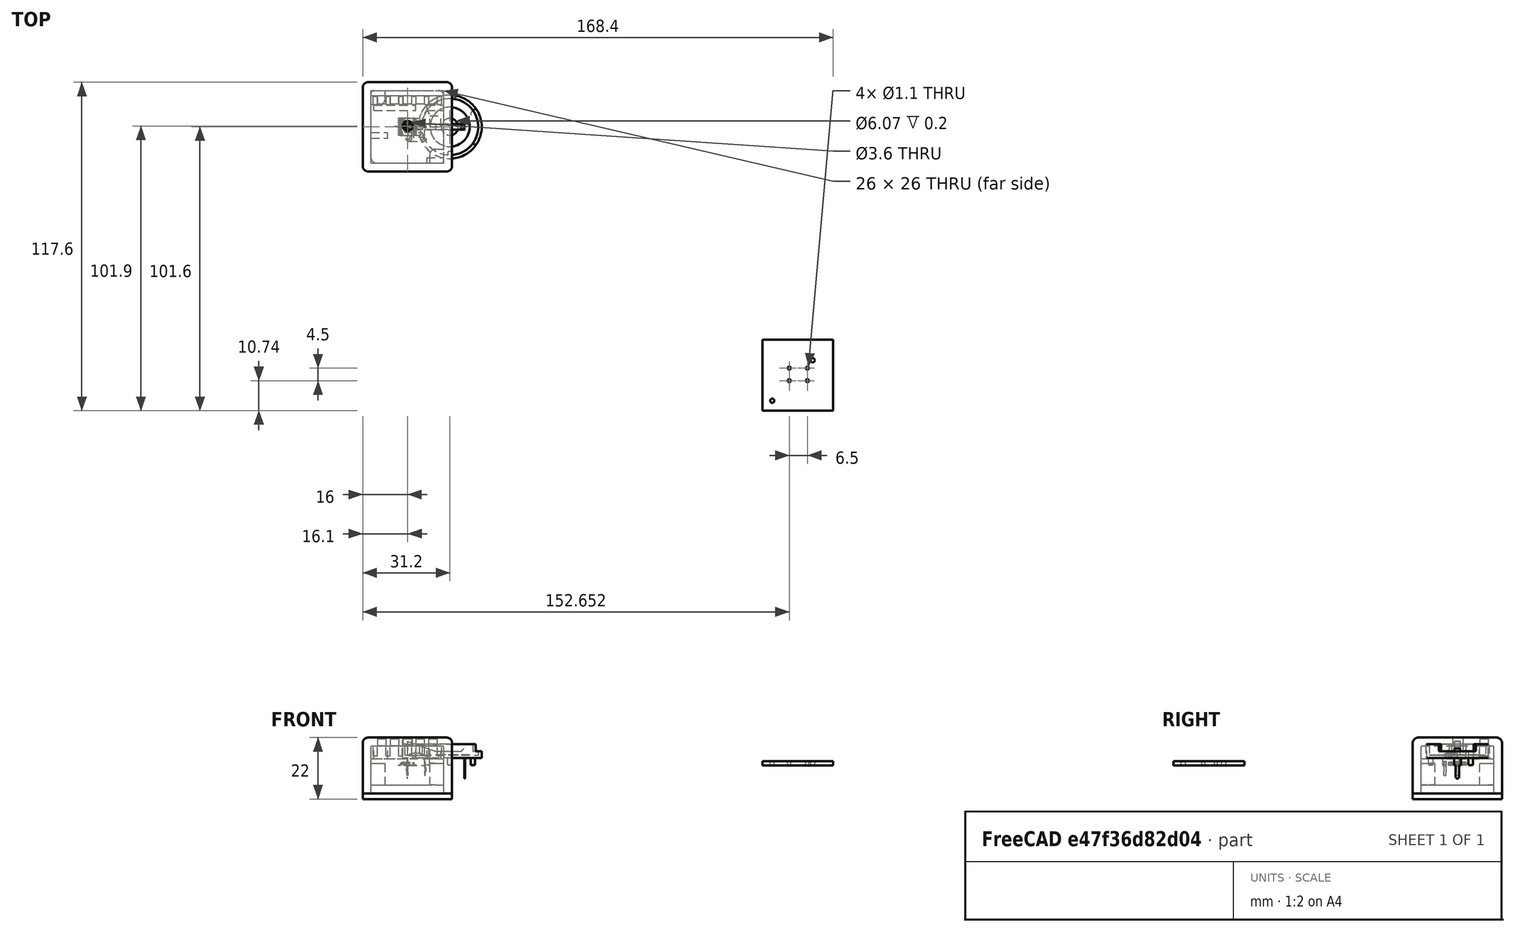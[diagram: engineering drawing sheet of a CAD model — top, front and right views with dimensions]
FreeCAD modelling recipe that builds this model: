
FCSTD DOCUMENT  (FreeCAD 0.18R16131 (Git))
Label: BoxSup
License: All rights reserved
LicenseURL: http://en.wikipedia.org/wiki/All_rights_reserved
objects: Part::Feature×30, App::Part×30, Part::Box×23, Part::Fillet×4, Part::Cut×3, Part::MultiFuse×3, Part::Cylinder×1
note: 64 computed .brp shape members not serialized (recipe doc carries the construction recipe); baked Part::Feature solids carry a one-line shape summary decoded from their .brp

FEATURE [Part::Box] Box  label="MainInside"
  AttacherType = Attacher::AttachEngine3D
  Height = 17
  Length = 26
  Placement = pos=(-13,-13,-10) rot=(0,0,1;0rad)
  Width = 26
FEATURE [Part::Box] Box001  label="MainOutside"
  AttacherType = Attacher::AttachEngine3D
  Height = 20
  Length = 32
  Placement = pos=(-16,-16,-10) rot=(0,0,1;0rad)
  Width = 32
FEATURE [Part::Feature] Part__Feature  label="SOLID"
  shape: bbox 2 x 1.25 x 1.1 mm, 50 faces (baked)
FEATURE [App::Part] LED_0805_2012Metric
  Group = -> [Part__Feature]
  License = CC BY 3.0
  LicenseURL = http://creativecommons.org/licenses/by/3.0/
  Origin = -> Origin
  Placement = pos=(144.272,-79.248,1.65) rot=(0,0,-1;1.5708rad)
FEATURE [Part::Feature] Part__Feature001  label="SOLID001"
  shape: bbox 7.174 x 6 x 7.8 mm, 105 faces (baked)
FEATURE [App::Part] SW_PUSH_6mm
  Group = -> [Part__Feature001]
  License = CC BY 3.0
  LicenseURL = http://creativecommons.org/licenses/by/3.0/
  Origin = -> Origin001
  Placement = pos=(136.652,-86.36,1.65) rot=(0,0,1;0rad)
FEATURE [Part::Feature] Part__Feature002  label="SOLID002"
  shape: bbox 1.6 x 0.8 x 0.45 mm, 26 faces (baked)
FEATURE [App::Part] R_0603_1608Metric
  Group = -> [Part__Feature002]
  License = CC BY 3.0
  LicenseURL = http://creativecommons.org/licenses/by/3.0/
  Origin = -> Origin002
  Placement = pos=(147.701,-98.679,1.65) rot=(0,0,1;0rad)
FEATURE [Part::Feature] Part__Feature003  label="SOLID003"
  shape: bbox 1.6 x 0.8 x 0.45 mm, 26 faces (baked)
FEATURE [App::Part] R_0603_1608Metric001
  Group = -> [Part__Feature003]
  License = CC BY 3.0
  LicenseURL = http://creativecommons.org/licenses/by/3.0/
  Origin = -> Origin003
  Placement = pos=(145.411,-99.187,1.65) rot=(0,0,1;1.5708rad)
FEATURE [Part::Feature] Part__Feature004  label="SOLID004"
  shape: bbox 6.4 x 6.5 x 1.2 mm, 336 faces (baked)
FEATURE [App::Part] TSSOP_20_4_4x6_5mm_P0_65mm
  Group = -> [Part__Feature004]
  License = CC BY 3.0
  LicenseURL = http://creativecommons.org/licenses/by/3.0/
  Origin = -> Origin004
  Placement = pos=(148.336,-93.81,1.65) rot=(0,0,1;1.5708rad)
FEATURE [Part::Feature] Part__Feature005  label="SOLID005"
  shape: bbox 2 x 1.25 x 1.1 mm, 50 faces (baked)
FEATURE [App::Part] LED_0805_2012Metric001
  Group = -> [Part__Feature005]
  License = CC BY 3.0
  LicenseURL = http://creativecommons.org/licenses/by/3.0/
  Origin = -> Origin005
  Placement = pos=(130.556,-79.248,1.65) rot=(0,0,-1;1.5708rad)
FEATURE [Part::Feature] Part__Feature006  label="SOLID006"
  shape: bbox 2 x 1.25 x 1.1 mm, 50 faces (baked)
FEATURE [App::Part] LED_0805_2012Metric002
  Group = -> [Part__Feature006]
  License = CC BY 3.0
  LicenseURL = http://creativecommons.org/licenses/by/3.0/
  Origin = -> Origin006
  Placement = pos=(135.128,-79.248,1.65) rot=(0,0,-1;1.5708rad)
FEATURE [Part::Feature] Part__Feature007  label="SOLID007"
  shape: bbox 2 x 1.25 x 1.1 mm, 50 faces (baked)
FEATURE [App::Part] LED_0805_2012Metric003
  Group = -> [Part__Feature007]
  License = CC BY 3.0
  LicenseURL = http://creativecommons.org/licenses/by/3.0/
  Origin = -> Origin007
  Placement = pos=(139.7,-79.248,1.65) rot=(0,0,-1;1.5708rad)
FEATURE [Part::Feature] Part__Feature008  label="SOLID008"
  shape: bbox 2 x 1.25 x 1.1 mm, 50 faces (baked)
FEATURE [App::Part] LED_0805_2012Metric004
  Group = -> [Part__Feature008]
  License = CC BY 3.0
  LicenseURL = http://creativecommons.org/licenses/by/3.0/
  Origin = -> Origin008
  Placement = pos=(148.844,-79.248,1.65) rot=(0,0,-1;1.5708rad)
FEATURE [Part::Feature] Part__Feature009  label="SOLID009"
  shape: bbox 1.6 x 0.8 x 0.45 mm, 26 faces (baked)
FEATURE [App::Part] R_0603_1608Metric002
  Group = -> [Part__Feature009]
  License = CC BY 3.0
  LicenseURL = http://creativecommons.org/licenses/by/3.0/
  Origin = -> Origin009
  Placement = pos=(132.588,-79.248,1.65) rot=(0,0,-1;1.5708rad)
FEATURE [Part::Feature] Part__Feature010  label="SOLID010"
  shape: bbox 1.6 x 0.8 x 0.45 mm, 26 faces (baked)
FEATURE [App::Part] R_0603_1608Metric003
  Group = -> [Part__Feature010]
  License = CC BY 3.0
  LicenseURL = http://creativecommons.org/licenses/by/3.0/
  Origin = -> Origin010
  Placement = pos=(137.16,-79.248,1.65) rot=(0,0,-1;1.5708rad)
FEATURE [Part::Feature] Part__Feature011  label="SOLID011"
  shape: bbox 1.6 x 0.8 x 0.45 mm, 26 faces (baked)
FEATURE [App::Part] R_0603_1608Metric004
  Group = -> [Part__Feature011]
  License = CC BY 3.0
  LicenseURL = http://creativecommons.org/licenses/by/3.0/
  Origin = -> Origin011
  Placement = pos=(141.732,-79.248,1.65) rot=(0,0,-1;1.5708rad)
FEATURE [Part::Feature] Part__Feature012  label="SOLID012"
  shape: bbox 1.6 x 0.8 x 0.45 mm, 26 faces (baked)
FEATURE [App::Part] R_0603_1608Metric005
  Group = -> [Part__Feature012]
  License = CC BY 3.0
  LicenseURL = http://creativecommons.org/licenses/by/3.0/
  Origin = -> Origin012
  Placement = pos=(146.304,-79.248,1.65) rot=(0,0,-1;1.5708rad)
FEATURE [Part::Feature] Part__Feature013  label="SOLID013"
  shape: bbox 1.6 x 0.8 x 0.45 mm, 26 faces (baked)
FEATURE [App::Part] R_0603_1608Metric006
  Group = -> [Part__Feature013]
  License = CC BY 3.0
  LicenseURL = http://creativecommons.org/licenses/by/3.0/
  Origin = -> Origin013
  Placement = pos=(150.876,-79.248,1.65) rot=(0,0,-1;1.5708rad)
FEATURE [Part::Feature] Part__Feature014  label="SOLID014"
  shape: bbox 1.6 x 0.8 x 0.8 mm, 28 faces (baked)
FEATURE [App::Part] C_0603_1608Metric
  Group = -> [Part__Feature014]
  License = CC BY 3.0
  LicenseURL = http://creativecommons.org/licenses/by/3.0/
  Origin = -> Origin014
  Placement = pos=(142.494,-94.488,1.65) rot=(0,0,-1;1.5708rad)
FEATURE [Part::Feature] Part__Feature015  label="SOLID015"
  shape: bbox 1.6 x 0.8 x 0.8 mm, 28 faces (baked)
FEATURE [App::Part] C_0603_1608Metric001
  Group = -> [Part__Feature015]
  License = CC BY 3.0
  LicenseURL = http://creativecommons.org/licenses/by/3.0/
  Origin = -> Origin015
  Placement = pos=(143.891,-94.488,1.65) rot=(0,0,-1;1.5708rad)
FEATURE [Part::Feature] Part__Feature016  label="SOLID016"
  shape: bbox 1.6 x 0.8 x 0.8 mm, 28 faces (baked)
FEATURE [App::Part] C_0603_1608Metric002
  Group = -> [Part__Feature016]
  License = CC BY 3.0
  LicenseURL = http://creativecommons.org/licenses/by/3.0/
  Origin = -> Origin016
  Placement = pos=(129.286,-95.631,1.65) rot=(0,0,1;0.785398rad)
FEATURE [Part::Feature] Part__Feature017  label="SOLID017"
  shape: bbox 1.6 x 0.8 x 0.8 mm, 28 faces (baked)
FEATURE [App::Part] C_0603_1608Metric003
  Group = -> [Part__Feature017]
  License = CC BY 3.0
  LicenseURL = http://creativecommons.org/licenses/by/3.0/
  Origin = -> Origin017
  Placement = pos=(128.778,-94.107,1.65) rot=(0,0,1;0.785398rad)
FEATURE [Part::Feature] Part__Feature018  label="SOLID018"
  shape: bbox 29.3 x 24.64 x 13.25 mm, 71 faces (baked)
FEATURE [App::Part] BatteryHolder_Keystone_103_1x20mm
  Group = -> [Part__Feature018]
  License = CC BY 3.0
  LicenseURL = http://creativecommons.org/licenses/by/3.0/
  Origin = -> Origin018
  Placement = pos=(130.556,-98.044,-0.05) rot=(0.92388,0.382683,0;3.14159rad)
FEATURE [Part::Feature] Part__Feature019  label="SOLID019"
  shape: bbox 2.5 x 3 x 1.2 mm, 76 faces (baked)
FEATURE [App::Part] SOT_23
  Group = -> [Part__Feature019]
  License = CC BY 3.0
  LicenseURL = http://creativecommons.org/licenses/by/3.0/
  Origin = -> Origin019
  Placement = pos=(130.81,-88.646,1.65) rot=(0,0,1;0rad)
FEATURE [Part::Feature] Part__Feature020  label="SOLID020"
  shape: bbox 2.5 x 3 x 1.2 mm, 76 faces (baked)
FEATURE [App::Part] SOT_23001
  Group = -> [Part__Feature020]
  License = CC BY 3.0
  LicenseURL = http://creativecommons.org/licenses/by/3.0/
  Origin = -> Origin020
  Placement = pos=(129.286,-85.09,1.65) rot=(0,0,1;3.14159rad)
FEATURE [Part::Feature] Part__Feature021  label="SOLID021"
  shape: bbox 1.6 x 0.8 x 0.45 mm, 26 faces (baked)
FEATURE [App::Part] R_0603_1608Metric007
  Group = -> [Part__Feature021]
  License = CC BY 3.0
  LicenseURL = http://creativecommons.org/licenses/by/3.0/
  Origin = -> Origin021
  Placement = pos=(128.27,-88.8745,1.65) rot=(0,0,1;1.5708rad)
FEATURE [Part::Feature] Part__Feature022  label="SOLID022"
  shape: bbox 1.6 x 0.8 x 0.45 mm, 26 faces (baked)
FEATURE [App::Part] R_0603_1608Metric008
  Group = -> [Part__Feature022]
  License = CC BY 3.0
  LicenseURL = http://creativecommons.org/licenses/by/3.0/
  Origin = -> Origin022
  Placement = pos=(131.699,-85.217,1.65) rot=(0,0,1;1.5708rad)
FEATURE [Part::Feature] Part__Feature023  label="SOLID023"
  shape: bbox 2.5 x 3 x 1.2 mm, 76 faces (baked)
FEATURE [App::Part] SOT_23002
  Group = -> [Part__Feature023]
  License = CC BY 3.0
  LicenseURL = http://creativecommons.org/licenses/by/3.0/
  Origin = -> Origin023
  Placement = pos=(135.89,-97.79,1.65) rot=(0,0,1;1.5708rad)
FEATURE [Part::Feature] Part__Feature024  label="SOLID024"
  shape: bbox 2.5 x 3 x 1.2 mm, 76 faces (baked)
FEATURE [App::Part] SOT_23003
  Group = -> [Part__Feature024]
  License = CC BY 3.0
  LicenseURL = http://creativecommons.org/licenses/by/3.0/
  Origin = -> Origin024
  Placement = pos=(139.446,-97.79,1.65) rot=(0,0,1;1.5708rad)
FEATURE [Part::Feature] Part__Feature025  label="SOLID025"
  shape: bbox 2.5 x 3 x 1.2 mm, 76 faces (baked)
FEATURE [App::Part] SOT_23004
  Group = -> [Part__Feature025]
  License = CC BY 3.0
  LicenseURL = http://creativecommons.org/licenses/by/3.0/
  Origin = -> Origin025
  Placement = pos=(143.002,-97.79,1.65) rot=(0,0,1;0rad)
FEATURE [Part::Feature] Part__Feature026  label="SOLID026"
  shape: bbox 1.6 x 0.8 x 0.45 mm, 26 faces (baked)
FEATURE [App::Part] R_0603_1608Metric009
  Group = -> [Part__Feature026]
  License = CC BY 3.0
  LicenseURL = http://creativecommons.org/licenses/by/3.0/
  Origin = -> Origin026
  Placement = pos=(135.89,-100.33,1.65) rot=(0,0,1;3.14159rad)
FEATURE [Part::Feature] Part__Feature027  label="SOLID027"
  shape: bbox 1.6 x 0.8 x 0.45 mm, 26 faces (baked)
FEATURE [App::Part] R_0603_1608Metric010
  Group = -> [Part__Feature027]
  License = CC BY 3.0
  LicenseURL = http://creativecommons.org/licenses/by/3.0/
  Origin = -> Origin027
  Placement = pos=(133.35,-99.5425,1.65) rot=(0,0,-1;1.5708rad)
FEATURE [Part::Feature] Part__Feature028  label="SOLID028"
  shape: bbox 1.6 x 0.8 x 0.45 mm, 26 faces (baked)
FEATURE [App::Part] R_0603_1608Metric011
  Group = -> [Part__Feature028]
  License = CC BY 3.0
  LicenseURL = http://creativecommons.org/licenses/by/3.0/
  Origin = -> Origin028
  Placement = pos=(139.192,-100.33,1.65) rot=(0,0,1;0rad)
FEATURE [Part::Feature] Part__Feature029  label="COMPOUND"
  shape: bbox 25.4 x 25.4 x 1.6 mm, 12 faces (baked)
FEATURE [App::Part] Open_CASCADE_STEP_translator_6_9_1
  Group = -> [LED_0805_2012Metric,SW_PUSH_6mm,R_0603_1608Metric,R_0603_1608Metric001,TSSOP_20_4_4x6_5mm_P0_65mm,LED_0805_2012Metric001,LED_0805_2012Metric002,LED_0805_2012Metric003,LED_0805_2012Metric004,R_0603_1608Metric002,R_0603_1608Metric003,R_0603_1608Metric004,R_0603_1608Metric005,R_0603_1608Metric006,C_0603_1608Metric,C_0603_1608Metric001,C_0603_1608Metric002,C_0603_1608Metric003,+12 more]
  License = CC BY 3.0
  LicenseURL = http://creativecommons.org/licenses/by/3.0/
  Origin = -> Origin029
  Placement = pos=(-139.7,88.9,0.8) rot=(0,0,1;0rad)
FEATURE [Part::Cut] Cut
  Base = -> Box001
  Tool = -> Box
FEATURE [Part::Box] Box002  label="L1"
  AttacherType = Attacher::AttachEngine3D
  Height = 3
  Length = 3
  Placement = pos=(-10.61,8.11,6.5) rot=(0,0,1;0rad)
  Width = 3
FEATURE [Part::Box] Box003  label="L2"
  AttacherType = Attacher::AttachEngine3D
  Height = 3
  Length = 3
  Placement = pos=(-6.04,8.11,6.5) rot=(0,0,1;0rad)
  Width = 3
FEATURE [Part::Box] Box004  label="L3"
  AttacherType = Attacher::AttachEngine3D
  Height = 3
  Length = 3
  Placement = pos=(-1.47,8.11,6.5) rot=(0,0,1;0rad)
  Width = 3
FEATURE [Part::Box] Box005  label="L4"
  AttacherType = Attacher::AttachEngine3D
  Height = 3
  Length = 3
  Placement = pos=(3.1,8.11,6.5) rot=(0,0,1;0rad)
  Width = 3
FEATURE [Part::Box] Box006  label="L5"
  AttacherType = Attacher::AttachEngine3D
  Height = 3
  Length = 3
  Placement = pos=(7.67,8.11,6.5) rot=(0,0,1;0rad)
  Width = 3
FEATURE [Part::Cylinder] Cylinder001  label="ButTouch"
  Angle = 360
  AttacherType = Attacher::AttachEngine3D
  Height = 3
  Placement = pos=(0.1,0.3,7) rot=(0,0,1;0rad)
  Radius = 1.8
FEATURE [Part::MultiFuse] Fusion
  Shapes = -> [Box002,Box006,Box005,Box003,Box004]
FEATURE [Part::Box] Box007  label="CubeDestek"
  AttacherType = Attacher::AttachEngine3D
  Height = 4.6
  Length = 26
  Placement = pos=(-13,11.2,2.4) rot=(0,0,1;0rad)
  Width = 1.8
FEATURE [Part::Box] Box008  label="CubeDestek2"
  AttacherType = Attacher::AttachEngine3D
  Height = 4.6
  Length = 4
  Placement = pos=(8,0,2.4) rot=(0,0,1;0rad)
  Width = 4
FEATURE [Part::Box] Box009  label="CubeDestek3"
  AttacherType = Attacher::AttachEngine3D
  Height = 4.6
  Length = 6
  Placement = pos=(-13,-4,2.4) rot=(0,0,1;0rad)
  Width = 2
FEATURE [Part::Box] Box010  label="CubeDestek4"
  AttacherType = Attacher::AttachEngine3D
  Height = 4.6
  Length = 6
  Placement = pos=(7,5.8,2.4) rot=(0,0,1;0rad)
  Width = 2
FEATURE [Part::Box] Box011  label="CubeDestek5"
  AttacherType = Attacher::AttachEngine3D
  Height = 4.6
  Length = 6
  Placement = pos=(7,-13,2.4) rot=(0,0,1;0rad)
  Width = 2
FEATURE [Part::Box] Box012  label="KapakGenis"
  AttacherType = Attacher::AttachEngine3D
  Height = 2
  Length = 32
  Placement = pos=(-16,-16,-12) rot=(0,0,1;0rad)
  Width = 32
FEATURE [Part::Box] Box013  label="KapakIc"
  AttacherType = Attacher::AttachEngine3D
  Height = 3
  Length = 26
  Placement = pos=(-13,-13,-10) rot=(0,0,1;0rad)
  Width = 26
FEATURE [Part::Box] Box014  label="KapakCikinti1"
  AttacherType = Attacher::AttachEngine3D
  Height = 7.8
  Length = 5
  Placement = pos=(-13,8,-7) rot=(0,0,1;0rad)
  Width = 5
FEATURE [Part::Box] Box015  label="KapakCikinti2"
  AttacherType = Attacher::AttachEngine3D
  Height = 7.8
  Length = 5
  Placement = pos=(8,-13,-7) rot=(0,0,1;0rad)
  Width = 5
FEATURE [Part::Cut] Cut001
  Base = -> Cut
  Tool = -> Fusion
FEATURE [Part::Cut] Cut002
  Base = -> Cut001
  Tool = -> Cylinder001
FEATURE [Part::Box] Box016  label="CubeDestek006"
  AttacherType = Attacher::AttachEngine3D
  Height = 4.6
  Length = 15
  Placement = pos=(-12,5.8,2.4) rot=(0,0,1;0rad)
  Width = 2
FEATURE [Part::Box] Box017  label="CubeDestek007"
  AttacherType = Attacher::AttachEngine3D
  Height = 3.5
  Length = 1.5
  Placement = pos=(1.55,8,3.5) rot=(0,0,1;0rad)
  Width = 3
FEATURE [Part::Box] Box018  label="CubeDestek008"
  AttacherType = Attacher::AttachEngine3D
  Height = 3.5
  Length = 1.5
  Placement = pos=(6.15,8,3.5) rot=(0,0,1;0rad)
  Width = 3
FEATURE [Part::Box] Box019  label="CubeDestek009"
  AttacherType = Attacher::AttachEngine3D
  Height = 3.5
  Length = 1.5
  Placement = pos=(-3.05,8,3.5) rot=(0,0,1;0rad)
  Width = 3
FEATURE [Part::Box] Box020  label="CubeDestek010"
  AttacherType = Attacher::AttachEngine3D
  Height = 3.5
  Length = 1.5
  Placement = pos=(-7.65,8,3.5) rot=(0,0,1;0rad)
  Width = 3
FEATURE [Part::Box] Box021  label="CubeDestek011"
  AttacherType = Attacher::AttachEngine3D
  Height = 3.5
  Length = 1.5
  Placement = pos=(-12.25,8,3.5) rot=(0,0,1;0rad)
  Width = 3
FEATURE [Part::Box] Box022  label="CubeDestek012"
  AttacherType = Attacher::AttachEngine3D
  Height = 3.5
  Length = 1.5
  Placement = pos=(10.75,8,3.5) rot=(0,0,1;0rad)
  Width = 3
FEATURE [Part::MultiFuse] Fusion001
  Shapes = -> [Box012,Box013,Box014,Box015]
FEATURE [Part::Fillet] Fillet
  Base = -> Fusion001
  Edges = 2 edges r=2: [Edge43,Edge47]
FEATURE [Part::Fillet] Fillet001
  Base = -> Fillet
  Edges = 2 edges r=1: [Edge38,Edge44]
FEATURE [Part::Fillet] Fillet002
  Base = -> Fillet001
  Edges = 6 edges r=2: [Edge5,Edge38,Edge52,Edge53,Edge56,Edge58]
FEATURE [Part::MultiFuse] Fusion002
  Shapes = -> [Box011,Box010,Box008,Box007,Box009,Box016,Box017,Box018,Box019,Box020,Box021,Box022]
FEATURE [Part::Fillet] Fillet003
  Base = -> Cut002
  Edges = 8 edges r=2: [Edge1,Edge2,Edge3,Edge6,Edge7,Edge8,Edge9,Edge12]
